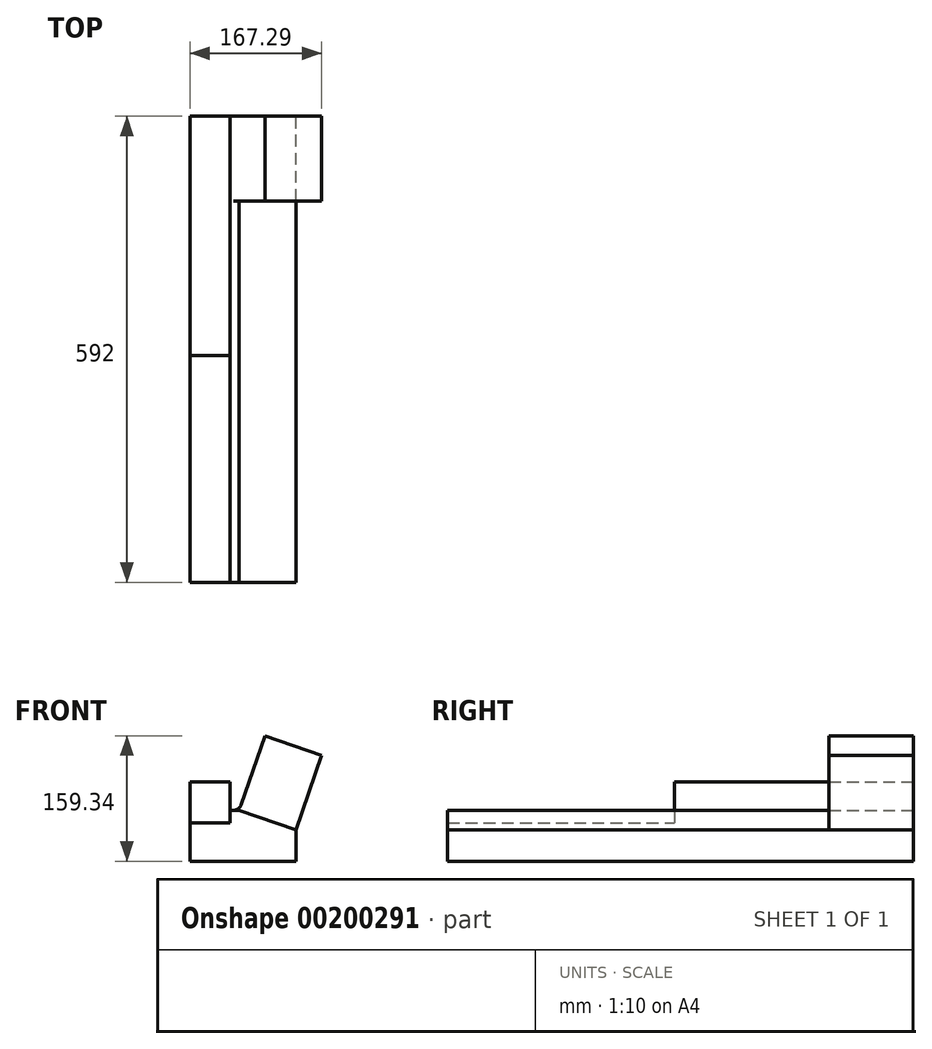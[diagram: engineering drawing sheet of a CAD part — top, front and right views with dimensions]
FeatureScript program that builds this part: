
annotation { "Feature Type Name" : "Feature", "Feature Type Description" : "" }
export const myFeature = defineFeature(function(context is Context, id is Id, definition is map)
    precondition{}
    {
        {
            var Q0;
            Q0=qCreatedBy(makeId("Front.planeOp"),FACE);
            var sketch = newSketch(context, id + "F0", { "sketchPlane" : qUnion([Q0])});
            skLineSegment(sketch, "E0.bottom", {"start": v(0, 0) * mm, "end": v(134.58, 0) * mm});
            skLineSegment(sketch, "E0.top", {"start": v(50.8, 64.84) * mm, "end": v(62.8, 64.84) * mm});
            skLineSegment(sketch, "E0.left", {"start": v(0, 0) * mm, "end": v(0, 48.84) * mm});
            skLineSegment(sketch, "E0.right", {"start": v(134.58, 0) * mm, "end": v(134.58, 40) * mm});
            skLineSegment(sketch, "E1", {"start": v(62.8, 64.84) * mm, "end": v(134.58, 40) * mm});
            skLineSegment(sketch, "E2", {"start": v(50.8, 64.84) * mm, "end": v(50.8, 48.84) * mm});
            skLineSegment(sketch, "E3", {"start": v(50.8, 48.84) * mm, "end": v(0, 48.84) * mm});
            skSolve(sketch);
        }
        {
            var Q0;
            Q0 = qSketchRegion(id + "F0", true);
            extrude(context, id + "F1", {"entities" : qUnion([Q0]), "depth" : 288 * mm});
        }
        {
            var Q0;
            Q0=qCreatedBy(makeId("Front.planeOp"),FACE);
            var sketch = newSketch(context, id + "F2", { "sketchPlane" : qUnion([Q0])});
            skLineSegment(sketch, "E4", {"start": v(134.58, 0) * mm, "end": v(134.58, 40) * mm});
            skLineSegment(sketch, "E5", {"start": v(134.58, 40) * mm, "end": v(62.8, 64.84) * mm});
            skLineSegment(sketch, "E6", {"start": v(62.8, 64.84) * mm, "end": v(0, 64.84) * mm});
            skLineSegment(sketch, "E7", {"start": v(0, 64.84) * mm, "end": v(0, 0) * mm});
            skLineSegment(sketch, "E8", {"start": v(0, 0) * mm, "end": v(134.58, 0) * mm});
            skSolve(sketch);
        }
        {
            var Q0;
            Q0 = qSketchRegion(id + "F2", true);
            extrude(context, id + "F3", {"entities" : qUnion([Q0]), "operationType" : NewBodyOperationType.ADD, "oppositeDirection" : true, "depth" : 304 * mm});
        }
        {
            var Q0;
            Q0=makeQuery(id+"F1.opExtrude","SWEPT_FACE",FACE,{"disambiguationData":[OSD([sQuery(id+"F0.wireOp",EDGE,"E3")])]});
            var sketch = newSketch(context, id + "F4", { "sketchPlane" : qUnion([Q0])});
            skLineSegment(sketch, "E9.bottom", {"start": v(50.8, -120.32) * mm, "end": v(21.45, -120.32) * mm});
            skLineSegment(sketch, "E9.top", {"start": v(50.8, 0) * mm, "end": v(21.45, 0) * mm});
            skLineSegment(sketch, "E9.left", {"start": v(50.8, -120.32) * mm, "end": v(50.8, 0) * mm});
            skLineSegment(sketch, "E9.right", {"start": v(21.45, -120.32) * mm, "end": v(21.45, 0) * mm});
            skSolve(sketch);
        }
        {
            var Q0;
            Q0=makeQuery(id+"F3.boolean.opBoolean","MERGE",FACE,{"derivedFrom":[makeQuery(id+"F1.opExtrude","SWEPT_FACE",FACE,{"disambiguationData":[OSD([sQuery(id+"F0.wireOp",EDGE,"E0.top")])]}),makeQuery(id+"F3.opExtrude","SWEPT_FACE",FACE,{"disambiguationData":[OSD([sQuery(id+"F2.wireOp",EDGE,"E6")])]})]});
            var sketch = newSketch(context, id + "F5", { "sketchPlane" : qUnion([Q0])});
            skLineSegment(sketch, "E10.bottom", {"start": v(50.8, 0) * mm, "end": v(0, 0) * mm});
            skLineSegment(sketch, "E10.top", {"start": v(50.8, 304) * mm, "end": v(0, 304) * mm});
            skLineSegment(sketch, "E10.left", {"start": v(50.8, 0) * mm, "end": v(50.8, 304) * mm});
            skLineSegment(sketch, "E10.right", {"start": v(0, 0) * mm, "end": v(0, 304) * mm});
            skSolve(sketch);
        }
        {
            var Q0;
            Q0 = qSketchRegion(id + "F5", true);
            extrude(context, id + "F6", {"entities" : qUnion([Q0]), "operationType" : NewBodyOperationType.ADD, "depth" : 36 * mm});
        }
        {
            var Q0;
            Q0=makeQuery(id+"F3.boolean.opBoolean","MERGE",FACE,{"derivedFrom":[makeQuery(id+"F1.opExtrude","SWEPT_FACE",FACE,{"disambiguationData":[OSD([sQuery(id+"F0.wireOp",EDGE,"E1")])]}),makeQuery(id+"F3.opExtrude","SWEPT_FACE",FACE,{"disambiguationData":[OSD([sQuery(id+"F2.wireOp",EDGE,"E5")])]})]});
            var sketch = newSketch(context, id + "F7", { "sketchPlane" : qUnion([Q0])});
            skLineSegment(sketch, "E11.bottom", {"start": v(38.14, 196.5) * mm, "end": v(114.1, 196.5) * mm});
            skLineSegment(sketch, "E11.top", {"start": v(38.14, 304) * mm, "end": v(114.1, 304) * mm});
            skLineSegment(sketch, "E11.left", {"start": v(38.14, 196.5) * mm, "end": v(38.14, 304) * mm});
            skLineSegment(sketch, "E11.right", {"start": v(114.1, 196.5) * mm, "end": v(114.1, 304) * mm});
            skSolve(sketch);
        }
        {
            var Q0;
            Q0 = qSketchRegion(id + "F7", true);
            extrude(context, id + "F8", {"entities" : qUnion([Q0]), "operationType" : NewBodyOperationType.ADD, "depth" : 100 * mm});
        }
        {
            var Q0;
            Q0=makeQuery(id+"F8.boolean.opBoolean","MERGE",EDGE,{"derivedFrom":[makeQuery(id+"F3.boolean.opBoolean","MERGE",EDGE,{"derivedFrom":[makeQuery(id+"F1.opExtrude","SWEPT_EDGE",EDGE,{"disambiguationData":[OSD([sQuery(id+"F0.wireOp",EDGE,"E0.top"),sQuery(id+"F0.wireOp",EDGE,"E1")])]}),makeQuery(id+"F3.opExtrude","SWEPT_EDGE",EDGE,{"disambiguationData":[OSD([sQuery(id+"F2.wireOp",EDGE,"E5"),sQuery(id+"F2.wireOp",EDGE,"E6")])]})]}),makeQuery(id+"F8.opExtrude","CAP_EDGE",EDGE,{"disambiguationData":[OSD([sQuery(id+"F7.wireOp",EDGE,"E11.left")])],"isStart":true})]});
            fillet(context, id + "F9", {"entities" : qUnion([Q0]), "radius" : 10 * mm, "tangentPropagation" : true, "allowEdgeOverflow" : false});
        }
    });
